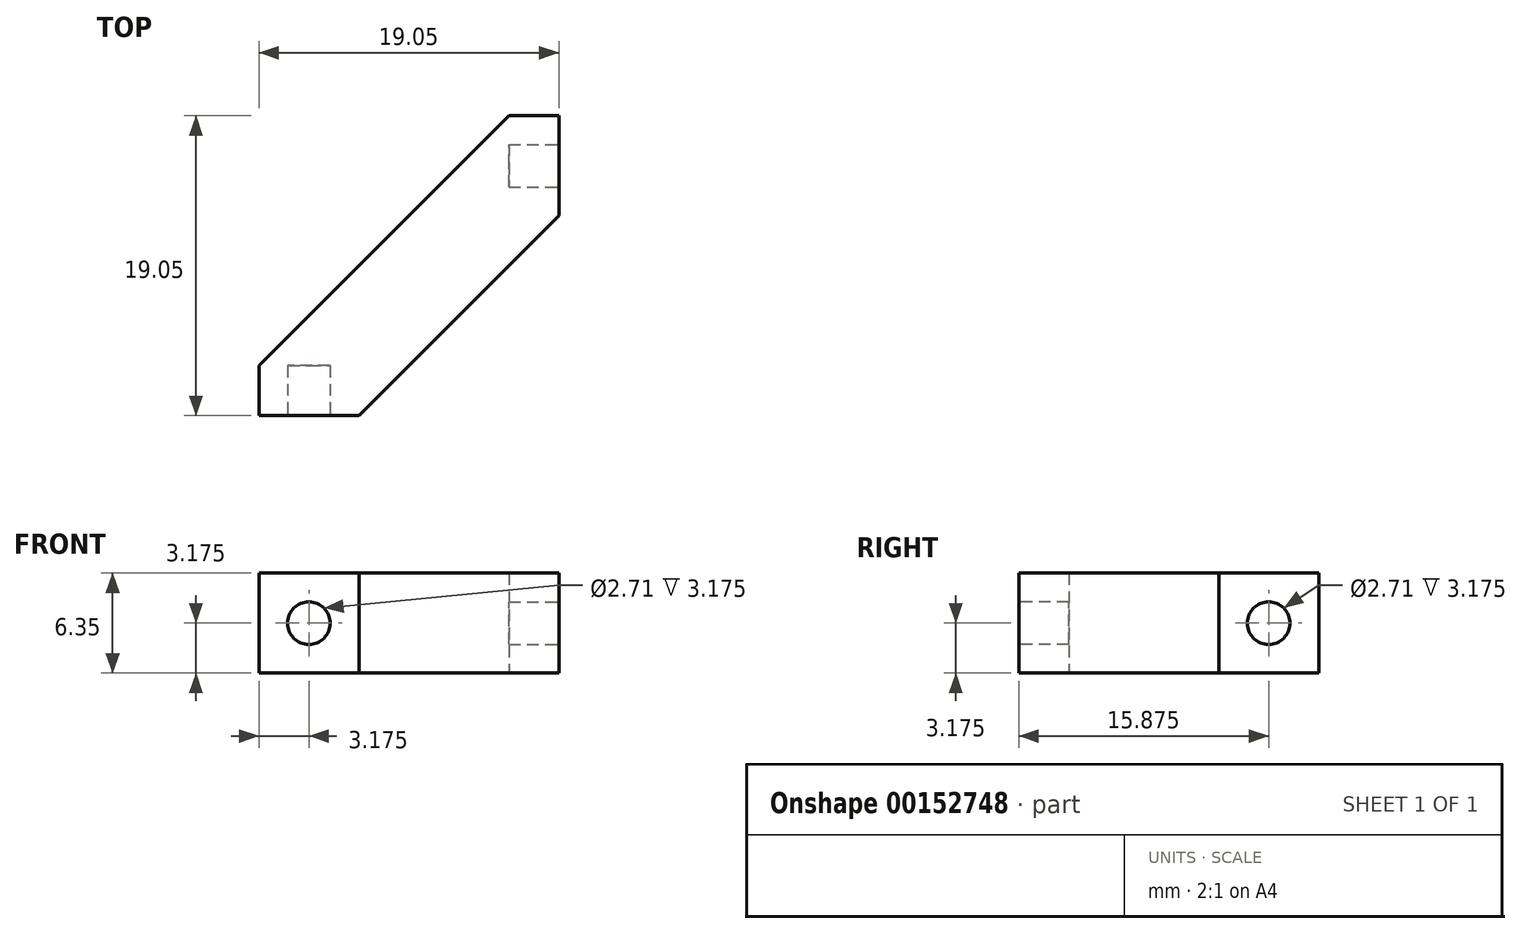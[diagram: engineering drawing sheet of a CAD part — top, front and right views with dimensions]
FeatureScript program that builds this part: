
annotation { "Feature Type Name" : "Feature", "Feature Type Description" : "" }
export const myFeature = defineFeature(function(context is Context, id is Id, definition is map)
    precondition{}
    {
        {
            var Q0;
            Q0=qCreatedBy(makeId("Top.planeOp"),FACE);
            var sketch = newSketch(context, id + "F0", { "sketchPlane" : qUnion([Q0])});
            skLineSegment(sketch, "E0.bottom", {"start": v(0, 0) * mm, "end": v(-12.7, 0) * mm, "construction": true});
            skLineSegment(sketch, "E0.left", {"start": v(0, 0) * mm, "end": v(0, 12.7) * mm, "construction": true});
            skLineSegment(sketch, "E1", {"start": v(-12.7, 0) * mm, "end": v(0, 12.7) * mm});
            skLineSegment(sketch, "E2", {"start": v(0, 12.7) * mm, "end": v(0, 19.05) * mm});
            skLineSegment(sketch, "E3", {"start": v(0, 19.05) * mm, "end": v(-3.18, 19.05) * mm});
            skLineSegment(sketch, "E4", {"start": v(-12.7, 0) * mm, "end": v(-19.05, 0) * mm});
            skLineSegment(sketch, "E5", {"start": v(-19.05, 0) * mm, "end": v(-19.05, 3.17) * mm});
            skLineSegment(sketch, "E6", {"start": v(-19.05, 3.17) * mm, "end": v(-3.17, 19.05) * mm});
            skSolve(sketch);
        }
        {
            var Q0;
            Q0 = qSketchRegion(id + "F0", true);
            extrude(context, id + "F1", {"entities" : qUnion([Q0]), "depth" : 6.35 * mm});
        }
        {
            var Q0;
            Q0=makeQuery(id+"F1.opExtrude","SWEPT_FACE",FACE,{"disambiguationData":[OSD([sQuery(id+"F0.wireOp",EDGE,"E2")])]});
            var sketch = newSketch(context, id + "F2", { "sketchPlane" : qUnion([Q0])});
            skLineSegment(sketch, "E7", {"start": v(19.05, 3.18) * mm, "end": v(12.7, 3.18) * mm, "construction": true});
            skCircle(sketch, "E8", {"center": v(15.88, 3.18) * mm, "radius": 1.35 * mm});
            skSolve(sketch);
        }
        {
            var Q0;
            Q0 = qSketchRegion(id + "F2", true);
            extrude(context, id + "F3", {"entities" : qUnion([Q0]), "operationType" : NewBodyOperationType.REMOVE, "oppositeDirection" : true, "depth" : 3.17 * mm});
        }
        {
            var Q0;
            Q0=makeQuery(id+"F1.opExtrude","SWEPT_FACE",FACE,{"disambiguationData":[OSD([sQuery(id+"F0.wireOp",EDGE,"E4")])]});
            var sketch = newSketch(context, id + "F4", { "sketchPlane" : qUnion([Q0])});
            skLineSegment(sketch, "E9", {"start": v(-19.05, 3.18) * mm, "end": v(-12.7, 3.18) * mm, "construction": true});
            skCircle(sketch, "E10", {"center": v(-15.88, 3.18) * mm, "radius": 1.35 * mm});
            skSolve(sketch);
        }
        {
            var Q0;
            Q0 = qSketchRegion(id + "F4", true);
            extrude(context, id + "F5", {"entities" : qUnion([Q0]), "operationType" : NewBodyOperationType.REMOVE, "oppositeDirection" : true, "depth" : 3.17 * mm});
        }
    });
